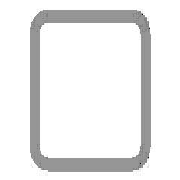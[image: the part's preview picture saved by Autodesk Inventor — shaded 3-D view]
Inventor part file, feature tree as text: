
AUTODESK INVENTOR PART (.ipt)
format: ipt  version: 2024 (Build 280153000, 153)  size: 150,016 bytes
history: native  units: mm (DEFAULTED — no unit token found)
features: other x4, plane x3, split x2, extrude x1, sketch x1
ambient origin geometry x8: Origin, YZ Plane, XZ Plane, XY Plane, X Axis, Y Axis, Z Axis, Center Point
bodies: Solid1 (feature_tree)
feature tree (11):
  parser-record x1  (decoder bookkeeping rows leaked as tree rows — omitted from the tree; the rows remain in map.json)
  other  "Driven Length"
  other  "Plano inicial"
  other  "Plano final"
  extrude  "Cuerpo"  TaperAngle=0.0deg  [1 undecoded]
  plane  "Plano de trabajo4"
  split  "Dividir1"
  plane  "Plano de trabajo5"
  split  "Dividir2"
  sketch  "Sketch3"  dims[d3=2940.8mm d4=0.0mm d10=50.8mm d11=50.8mm d12=3.175mm d13=-25.4mm d14=2915.4mm d15=25.4mm d16=25.4mm d17=6.35mm d18=90.0deg d19=2940.8mm]
  plane  "Work Plane3"
note: 1 required parameter value undecoded (feature->parameter linkage not recoverable at this tier; creation-order binding heuristic only, values carry confidence <= 0.55)
